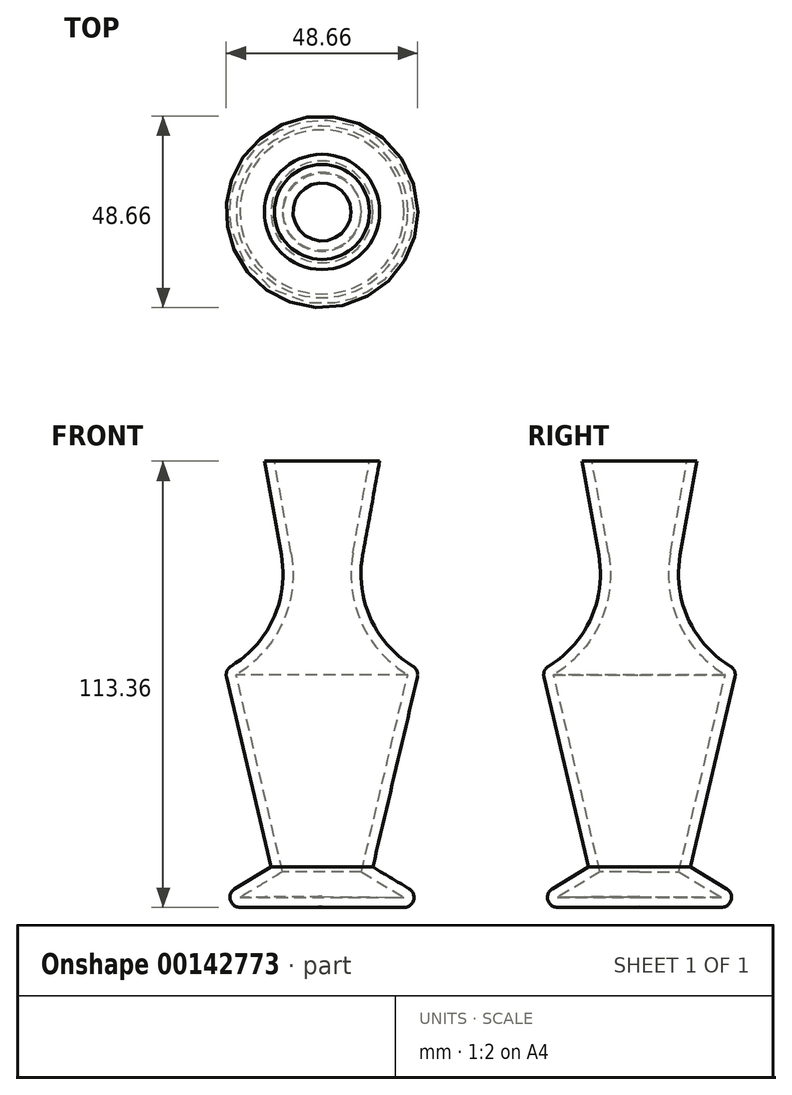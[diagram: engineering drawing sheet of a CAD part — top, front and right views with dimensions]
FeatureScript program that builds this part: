
annotation { "Feature Type Name" : "Feature", "Feature Type Description" : "" }
export const myFeature = defineFeature(function(context is Context, id is Id, definition is map)
    precondition{}
    {
        {
            var Q0;
            Q0=qCreatedBy(makeId("Front.planeOp"),FACE);
            var sketch = newSketch(context, id + "F0", { "sketchPlane" : qUnion([Q0])});
            skLineSegment(sketch, "E0", {"start": v(0, 53) * mm, "end": v(0, -60.17) * mm});
            skLineSegment(sketch, "E1", {"start": v(0, 53) * mm, "end": v(-14.65, 53) * mm});
            skLineSegment(sketch, "E2", {"start": v(-14.65, 53) * mm, "end": v(-10.34, 29.15) * mm});
            skArc(sketch, "E3", {"start": v(-23.1, 0.9) * mm, "mid": v(-12.33, 13.04) * mm, "end": v(-10.34, 29.15) * mm});
            skLineSegment(sketch, "E4", {"start": v(-24.26, -1.86) * mm, "end": v(-12.93, -50.12) * mm});
            skLineSegment(sketch, "E5", {"start": v(-12.93, -50.12) * mm, "end": v(-22.15, -55.65) * mm});
            skLineSegment(sketch, "E6", {"start": v(-20.82, -60.37) * mm, "end": v(0, -60.17) * mm});
            skPoint(sketch, "E7.visualSharp", {"position": v(-24.7, 0) * mm});
            skArc(sketch, "E7.filletArc", {"start": v(-23.1, 0.9) * mm, "mid": v(-24.13, -0.3) * mm, "end": v(-24.26, -1.86) * mm});
            skPoint(sketch, "E8.visualSharp", {"position": v(-30.16, -60.46) * mm});
            skArc(sketch, "E8.filletArc", {"start": v(-22.15, -55.65) * mm, "mid": v(-23.29, -58.52) * mm, "end": v(-20.82, -60.37) * mm});
            skSolve(sketch);
        }
        {
            var Q0;
            Q0 = qSketchRegion(id + "F0", true);
            var Q1;
            Q1=sQuery(id+"F0.wireOp",EDGE,"E0");
            revolve(context, id + "F1", {"entities" : qUnion([Q0]), "axis" : qUnion([Q1]), "revolveType" : RevolveType.FULL});
        }
        {
            var Q0;
            Q0=makeQuery(id+"F1.opRevolve","SWEPT_FACE",FACE,{"disambiguationData":[OSD([sQuery(id+"F0.wireOp",EDGE,"E1")])]});
            shell(context, id + "F2", {"entities" : qUnion([Q0]), "thickness" : 2.54 * mm});
        }
    });
